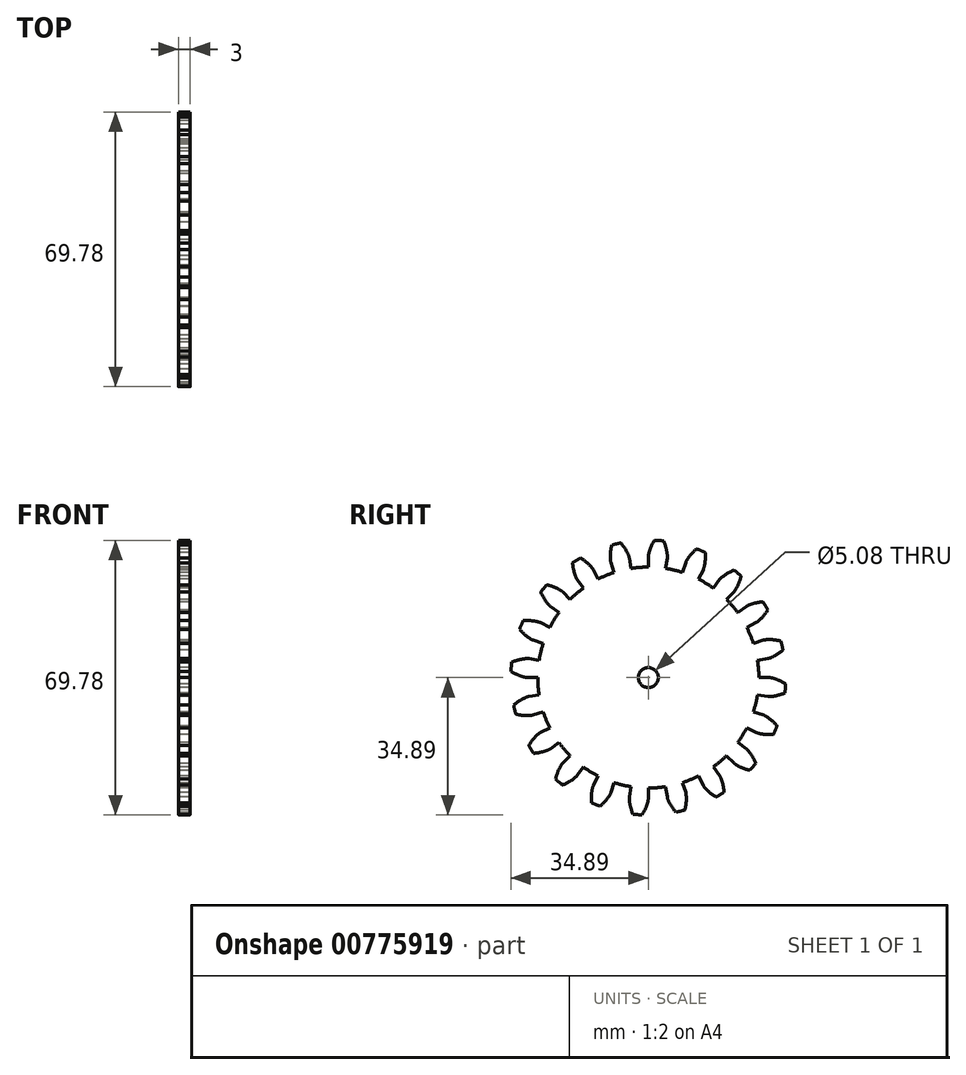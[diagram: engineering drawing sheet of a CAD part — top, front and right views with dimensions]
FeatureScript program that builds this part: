
annotation { "Feature Type Name" : "Feature", "Feature Type Description" : "" }
export const myFeature = defineFeature(function(context is Context, id is Id, definition is map)
    precondition{}
    {
        {
            assignVariable(context, id + "F0", {"name" : "NumberTeeth", "anyValue" : 20});
        }
        {
            assignVariable(context, id + "F1", {"name" : "GearThickness", "anyValue" : 3});
        }
        {
            var Q0;
            Q0=qCreatedBy(makeId("Right.planeOp"),FACE);
            var sketch = newSketch(context, id + "F2", { "sketchPlane" : qUnion([Q0])});
            skCircle(sketch, "E0", {"center": v(0, 0) * mm, "radius": 28.08 * mm});
            skCircle(sketch, "E1", {"center": v(0, 0) * mm, "radius": 30.74 * mm, "construction": true});
            skCircle(sketch, "E2", {"center": v(0, 0) * mm, "radius": 31.75 * mm, "construction": true});
            skCircle(sketch, "E3", {"center": v(0, 0) * mm, "radius": 34.93 * mm});
            skLineSegment(sketch, "E4", {"start": v(0, 0) * mm, "end": v(-30.74, 0) * mm, "construction": true});
            skLineSegment(sketch, "E5.1.0", {"start": v(0, 0) * mm, "end": v(-30.7, 1.54) * mm, "construction": true});
            skLineSegment(sketch, "E5.2.0", {"start": v(0, 0) * mm, "end": v(-30.59, 3.07) * mm, "construction": true});
            skLineSegment(sketch, "E5.3.0", {"start": v(0, 0) * mm, "end": v(-30.4, 4.6) * mm, "construction": true});
            skLineSegment(sketch, "E5.4.0", {"start": v(0, 0) * mm, "end": v(-30.13, 6.1) * mm, "construction": true});
            skLineSegment(sketch, "E5.5.0", {"start": v(0, 0) * mm, "end": v(-29.78, 7.6) * mm, "construction": true});
            skLineSegment(sketch, "E5.6.0", {"start": v(0, 0) * mm, "end": v(-29.37, 9.08) * mm, "construction": true});
            skLineSegment(sketch, "E5.7.0", {"start": v(0, 0) * mm, "end": v(-28.88, 10.54) * mm, "construction": true});
            skLineSegment(sketch, "E5.8.0", {"start": v(0, 0) * mm, "end": v(-28.31, 11.97) * mm, "construction": true});
            skLineSegment(sketch, "E5.9.0", {"start": v(0, 0) * mm, "end": v(-27.68, 13.37) * mm, "construction": true});
            skLineSegment(sketch, "E5.10.0", {"start": v(0, 0) * mm, "end": v(-26.98, 14.74) * mm, "construction": true});
            skLineSegment(sketch, "E5.11.0", {"start": v(0, 0) * mm, "end": v(-26.2, 16.07) * mm, "construction": true});
            skLineSegment(sketch, "E5.12.0", {"start": v(0, 0) * mm, "end": v(-25.37, 17.36) * mm, "construction": true});
            skLineSegment(sketch, "E5.13.0", {"start": v(0, 0) * mm, "end": v(-24.47, 18.6) * mm, "construction": true});
            skLineSegment(sketch, "E5.14.0", {"start": v(0, 0) * mm, "end": v(-23.51, 19.8) * mm, "construction": true});
            skLineSegment(sketch, "E5.anchor2", {"start": v(0, 0) * mm, "end": v(-23.51, 19.8) * mm, "construction": true});
            skLineSegment(sketch, "E6", {"start": v(-30.7, 1.54) * mm, "end": v(-30.78, 0) * mm, "construction": true});
            skLineSegment(sketch, "E7", {"start": v(-30.59, 3.07) * mm, "end": v(-30.9, 0.01) * mm, "construction": true});
            skLineSegment(sketch, "E8", {"start": v(-30.4, 4.6) * mm, "end": v(-31.08, 0.03) * mm, "construction": true});
            skLineSegment(sketch, "E9", {"start": v(-29.78, 7.6) * mm, "end": v(-31.68, 0.16) * mm, "construction": true});
            skLineSegment(sketch, "E10", {"start": v(-29.37, 9.08) * mm, "end": v(-32.1, 0.27) * mm, "construction": true});
            skLineSegment(sketch, "E11", {"start": v(-28.88, 10.54) * mm, "end": v(-32.56, 0.43) * mm, "construction": true});
            skLineSegment(sketch, "E12", {"start": v(-28.31, 11.97) * mm, "end": v(-33.1, 0.65) * mm, "construction": true});
            skLineSegment(sketch, "E13", {"start": v(-27.68, 13.37) * mm, "end": v(-33.7, 0.91) * mm, "construction": true});
            skLineSegment(sketch, "E14", {"start": v(-26.98, 14.74) * mm, "end": v(-34.34, 1.25) * mm, "construction": true});
            skLineSegment(sketch, "E15", {"start": v(-26.2, 16.07) * mm, "end": v(-35.04, 1.65) * mm, "construction": true});
            skLineSegment(sketch, "E16", {"start": v(-30.13, 6.1) * mm, "end": v(-31.35, 0.08) * mm, "construction": true});
            skLineSegment(sketch, "E17", {"start": v(-25.37, 17.36) * mm, "end": v(-35.78, 2.13) * mm, "construction": true});
            skLineSegment(sketch, "E18", {"start": v(-24.47, 18.6) * mm, "end": v(-36.56, 2.7) * mm, "construction": true});
            skLineSegment(sketch, "E19", {"start": v(-23.51, 19.8) * mm, "end": v(-37.37, 3.35) * mm, "construction": true});
            skLineSegment(sketch, "E20", {"start": v(0, 0) * mm, "end": v(-30.64, 2.41) * mm, "construction": true});
            skLineSegment(sketch, "E21", {"start": v(-28.08, 0) * mm, "end": v(-30.74, 0) * mm});
            skLineSegment(sketch, "E22.MirrorCS", {"start": v(-27.73, 4.4) * mm, "end": v(-30.36, 4.8) * mm});
            skFitSpline(sketch, "E23", {"points": [v(-30.74, 0) * mm, v(-30.78, 0) * mm, v(-30.9, 0.01) * mm, v(-31.08, 0.03) * mm, v(-31.35, 0.08) * mm, v(-31.68, 0.16) * mm, v(-32.1, 0.27) * mm, v(-32.56, 0.43) * mm, v(-33.1, 0.65) * mm, v(-33.7, 0.91) * mm, v(-34.34, 1.25) * mm, v(-35.04, 1.65) * mm, v(-35.78, 2.13) * mm, v(-36.56, 2.7) * mm, v(-37.37, 3.35) * mm], "startDerivative": vector(-0.71, 0) * mm, "endDerivative": vector(-1.6, 1.36) * mm});
            skLineSegment(sketch, "E24", {"start": v(-25.97, -6.26) * mm, "end": v(-37.37, 3.35) * mm, "construction": true});
            skFitSpline(sketch, "E25.MirrorCS", {"points": [v(-30.36, 4.8) * mm, v(-30.4, 4.81) * mm, v(-30.51, 4.82) * mm, v(-30.7, 4.83) * mm, v(-30.97, 4.82) * mm, v(-31.32, 4.8) * mm, v(-31.74, 4.75) * mm, v(-32.23, 4.67) * mm, v(-32.8, 4.54) * mm, v(-33.42, 4.37) * mm, v(-34.12, 4.14) * mm, v(-34.87, 3.85) * mm, v(-35.68, 3.49) * mm, v(-36.53, 3.06) * mm, v(-37.44, 2.54) * mm], "startDerivative": vector(-0.7, 0.11) * mm, "endDerivative": vector(-1.8, -1.09) * mm});
            skCircle(sketch, "E26", {"center": v(0, 0) * mm, "radius": 2.54 * mm});
            skSolve(sketch);
        }
        {
            var Q0;
            {var subQ0=sQuery(id+"F2.wireOp",EDGE,"E0");var subQ27=makeQuery(id+"F2.imprint","INTERSECT",VERTEX,{"derivedFrom":[subQ0,sQuery(id+"F2.wireOp",EDGE,"10ea1024-8cf5-41f5-a75f-a634b86921f3.10.0")]});Q0=makeQuery(id+"F2.imprint","IMPRINT",FACE,{"disambiguationData":[TD([[makeQuery(id+"F2.imprint","IMPRINT",EDGE,{"disambiguationData":[TD([[subQ27,-1.0]])],"derivedFrom":subQ0}),1.0]])]});}
            var Q1;
            {var subQ0=sQuery(id+"F2.wireOp",EDGE,"10ea1024-8cf5-41f5-a75f-a634b86921f3.1.0");Q1=makeQuery(id+"F2.imprint","IMPRINT",FACE,{"disambiguationData":[TD([[makeQuery(id+"F2.imprint","IMPRINT",EDGE,{"derivedFrom":subQ0}),-1.0]])]});}
            var Q2;
            {var subQ7=sQuery(id+"F2.wireOp",EDGE,"10ea1024-8cf5-41f5-a75f-a634b86921f3.2.0");Q2=makeQuery(id+"F2.imprint","IMPRINT",FACE,{"disambiguationData":[TD([[makeQuery(id+"F2.imprint","IMPRINT",EDGE,{"derivedFrom":subQ7}),-1.0]])]});}
            var Q3;
            {var subQ8=sQuery(id+"F2.wireOp",EDGE,"10ea1024-8cf5-41f5-a75f-a634b86921f3.3.0");Q3=makeQuery(id+"F2.imprint","IMPRINT",FACE,{"disambiguationData":[TD([[makeQuery(id+"F2.imprint","IMPRINT",EDGE,{"derivedFrom":subQ8}),-1.0]])]});}
            var Q4;
            {var subQ2=sQuery(id+"F2.wireOp",EDGE,"10ea1024-8cf5-41f5-a75f-a634b86921f3.4.0");Q4=makeQuery(id+"F2.imprint","IMPRINT",FACE,{"disambiguationData":[TD([[makeQuery(id+"F2.imprint","IMPRINT",EDGE,{"derivedFrom":subQ2}),-1.0]])]});}
            var Q5;
            {var subQ8=sQuery(id+"F2.wireOp",EDGE,"10ea1024-8cf5-41f5-a75f-a634b86921f3.5.0");Q5=makeQuery(id+"F2.imprint","IMPRINT",FACE,{"disambiguationData":[TD([[makeQuery(id+"F2.imprint","IMPRINT",EDGE,{"derivedFrom":subQ8}),-1.0]])]});}
            var Q6;
            {var subQ3=sQuery(id+"F2.wireOp",EDGE,"10ea1024-8cf5-41f5-a75f-a634b86921f3.6.0");Q6=makeQuery(id+"F2.imprint","IMPRINT",FACE,{"disambiguationData":[TD([[makeQuery(id+"F2.imprint","IMPRINT",EDGE,{"derivedFrom":subQ3}),-1.0]])]});}
            var Q7;
            {var subQ0=sQuery(id+"F2.wireOp",EDGE,"10ea1024-8cf5-41f5-a75f-a634b86921f3.7.0");Q7=makeQuery(id+"F2.imprint","IMPRINT",FACE,{"disambiguationData":[TD([[makeQuery(id+"F2.imprint","IMPRINT",EDGE,{"derivedFrom":subQ0}),-1.0]])]});}
            var Q8;
            {var subQ5=sQuery(id+"F2.wireOp",EDGE,"10ea1024-8cf5-41f5-a75f-a634b86921f3.8.0");Q8=makeQuery(id+"F2.imprint","IMPRINT",FACE,{"disambiguationData":[TD([[makeQuery(id+"F2.imprint","IMPRINT",EDGE,{"derivedFrom":subQ5}),-1.0]])]});}
            var Q9;
            {var subQ1=sQuery(id+"F2.wireOp",EDGE,"10ea1024-8cf5-41f5-a75f-a634b86921f3.9.0");Q9=makeQuery(id+"F2.imprint","IMPRINT",FACE,{"disambiguationData":[TD([[makeQuery(id+"F2.imprint","IMPRINT",EDGE,{"derivedFrom":subQ1}),-1.0]])]});}
            var Q10;
            {var subQ5=sQuery(id+"F2.wireOp",EDGE,"10ea1024-8cf5-41f5-a75f-a634b86921f3.10.0");Q10=makeQuery(id+"F2.imprint","IMPRINT",FACE,{"disambiguationData":[TD([[makeQuery(id+"F2.imprint","IMPRINT",EDGE,{"derivedFrom":subQ5}),-1.0]])]});}
            var Q11;
            {var subQ8=sQuery(id+"F2.wireOp",EDGE,"10ea1024-8cf5-41f5-a75f-a634b86921f3.11.0");Q11=makeQuery(id+"F2.imprint","IMPRINT",FACE,{"disambiguationData":[TD([[makeQuery(id+"F2.imprint","IMPRINT",EDGE,{"derivedFrom":subQ8}),-1.0]])]});}
            var Q12;
            {var subQ2=sQuery(id+"F2.wireOp",EDGE,"10ea1024-8cf5-41f5-a75f-a634b86921f3.12.0");Q12=makeQuery(id+"F2.imprint","IMPRINT",FACE,{"disambiguationData":[TD([[makeQuery(id+"F2.imprint","IMPRINT",EDGE,{"derivedFrom":subQ2}),-1.0]])]});}
            var Q13;
            {var subQ3=sQuery(id+"F2.wireOp",EDGE,"10ea1024-8cf5-41f5-a75f-a634b86921f3.13.0");Q13=makeQuery(id+"F2.imprint","IMPRINT",FACE,{"disambiguationData":[TD([[makeQuery(id+"F2.imprint","IMPRINT",EDGE,{"derivedFrom":subQ3}),-1.0]])]});}
            var Q14;
            {var subQ0=sQuery(id+"F2.wireOp",EDGE,"10ea1024-8cf5-41f5-a75f-a634b86921f3.14.0");Q14=makeQuery(id+"F2.imprint","IMPRINT",FACE,{"disambiguationData":[TD([[makeQuery(id+"F2.imprint","IMPRINT",EDGE,{"derivedFrom":subQ0}),-1.0]])]});}
            var Q15;
            {var subQ6=sQuery(id+"F2.wireOp",EDGE,"10ea1024-8cf5-41f5-a75f-a634b86921f3.15.0");Q15=makeQuery(id+"F2.imprint","IMPRINT",FACE,{"disambiguationData":[TD([[makeQuery(id+"F2.imprint","IMPRINT",EDGE,{"derivedFrom":subQ6}),-1.0]])]});}
            var Q16;
            {var subQ5=sQuery(id+"F2.wireOp",EDGE,"10ea1024-8cf5-41f5-a75f-a634b86921f3.16.0");Q16=makeQuery(id+"F2.imprint","IMPRINT",FACE,{"disambiguationData":[TD([[makeQuery(id+"F2.imprint","IMPRINT",EDGE,{"derivedFrom":subQ5}),-1.0]])]});}
            var Q17;
            {var subQ7=sQuery(id+"F2.wireOp",EDGE,"10ea1024-8cf5-41f5-a75f-a634b86921f3.17.0");Q17=makeQuery(id+"F2.imprint","IMPRINT",FACE,{"disambiguationData":[TD([[makeQuery(id+"F2.imprint","IMPRINT",EDGE,{"derivedFrom":subQ7}),-1.0]])]});}
            var Q18;
            {var subQ5=sQuery(id+"F2.wireOp",EDGE,"10ea1024-8cf5-41f5-a75f-a634b86921f3.18.0");Q18=makeQuery(id+"F2.imprint","IMPRINT",FACE,{"disambiguationData":[TD([[makeQuery(id+"F2.imprint","IMPRINT",EDGE,{"derivedFrom":subQ5}),-1.0]])]});}
            var Q19;
            {var subQ8=sQuery(id+"F2.wireOp",EDGE,"10ea1024-8cf5-41f5-a75f-a634b86921f3.19.0");Q19=makeQuery(id+"F2.imprint","IMPRINT",FACE,{"disambiguationData":[TD([[makeQuery(id+"F2.imprint","IMPRINT",EDGE,{"derivedFrom":subQ8}),-1.0]])]});}
            var Q20;
            {var subQ8=sQuery(id+"F2.wireOp",EDGE,"E21");Q20=makeQuery(id+"F2.imprint","IMPRINT",FACE,{"disambiguationData":[TD([[makeQuery(id+"F2.imprint","IMPRINT",EDGE,{"derivedFrom":subQ8}),-1.0]])]});}
            extrude(context, id + "F3", {"entities" : qUnion([Q0, Q1, Q2, Q3, Q4, Q5, Q6, Q7, Q8, Q9, Q10, Q11, Q12, Q13, Q14, Q15, Q16, Q17, Q18, Q19, Q20]), "depth" : (getVariable(context, 'GearThickness')) * mm});
        }
        {
            var Q0;
            Q0=makeQuery(id+"F3.opExtrude","SWEPT_FACE",FACE,{"disambiguationData":[OSD([sQuery(id+"F2.wireOp",EDGE,"E25.MirrorCS")])]});
            var Q1;
            Q1=makeQuery(id+"F3.opExtrude","SWEPT_FACE",FACE,{"disambiguationData":[OSD([sQuery(id+"F2.wireOp",EDGE,"E23")])]});
            var Q2;
            Q2=makeQuery(id+"F3.opExtrude","SWEPT_FACE",FACE,{"disambiguationData":[OSD([sQuery(id+"F2.wireOp",EDGE,"E3")])]});
            var Q3;
            Q3=makeQuery(id+"F3.opExtrude","SWEPT_FACE",FACE,{"disambiguationData":[OSD([sQuery(id+"F2.wireOp",EDGE,"E22.MirrorCS")])]});
            var Q4;
            Q4=makeQuery(id+"F3.opExtrude","SWEPT_FACE",FACE,{"disambiguationData":[OSD([sQuery(id+"F2.wireOp",EDGE,"E21")])]});
            var Q5;
            Q5=makeQuery(id+"F3.opExtrude","SWEPT_FACE",FACE,{"disambiguationData":[OSD([sQuery(id+"F2.wireOp",EDGE,"E0")])]});
            circularPattern(context, id + "F4", {"faces" : qUnion([Q0, Q1, Q2, Q3, Q4]), "axis" : qUnion([Q5]), "angle" : 360 * degree, "instanceCount" : getVariable(context, 'NumberTeeth'), "equalSpace" : true, "patternType" : PatternType.FACE});
        }
    });
